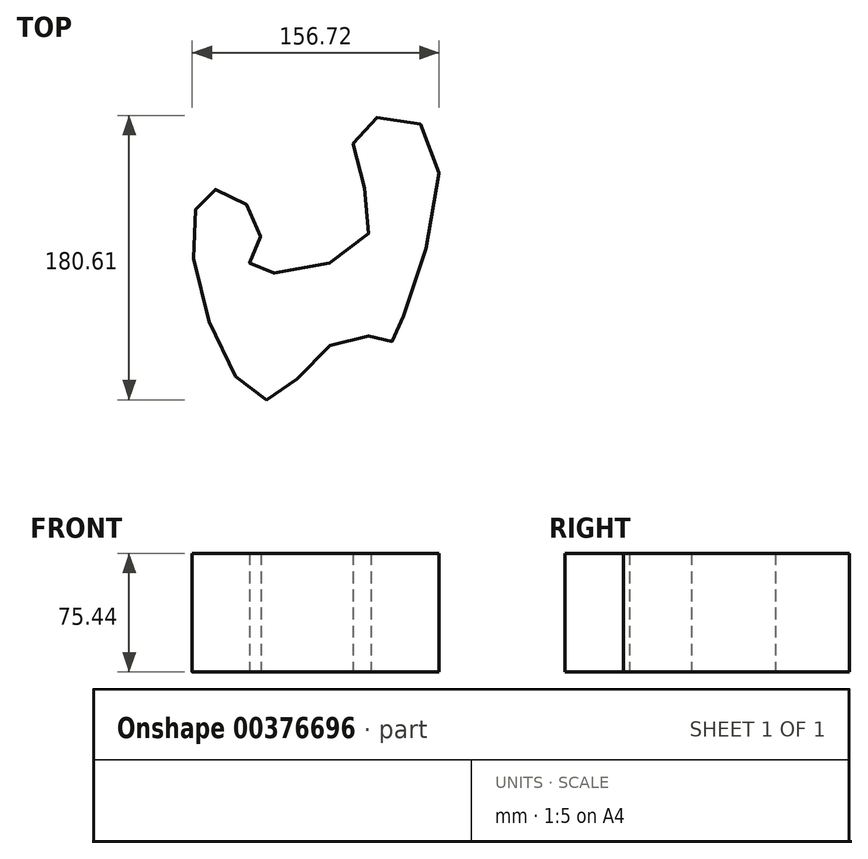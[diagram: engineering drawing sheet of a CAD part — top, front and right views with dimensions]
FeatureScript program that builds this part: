
annotation { "Feature Type Name" : "Feature", "Feature Type Description" : "" }
export const myFeature = defineFeature(function(context is Context, id is Id, definition is map)
    precondition{}
    {
        {
            var Q0;
            Q0=qCreatedBy(makeId("Top.planeOp"),FACE);
            var sketch = newSketch(context, id + "F0", { "sketchPlane" : qUnion([Q0])});
            skFitSpline(sketch, "E0", {"points": [v(-137.83, -57.14) * mm, v(-123.76, -13.3) * mm, v(-95.1, -40.71) * mm, v(-101.2, -63.47) * mm, v(-28.09, -44.15) * mm, v(-34.93, 22.42) * mm, v(13.54, 20.18) * mm, v(-11.02, -109.4) * mm, v(-11.71, -109.8) * mm, v(-44.48, -108.57) * mm, v(-91.93, -146.96) * mm, v(-137.83, -57.14) * mm]});
            skSolve(sketch);
        }
        {
            var Q0;
            Q0=makeQuery(id+"F0.imprint","IMPRINT",FACE,{"disambiguationData":[TD([[makeQuery(id+"F0.imprint","IMPRINT",EDGE,{"derivedFrom":sQuery(id+"F0.wireOp",EDGE,"E0")}),-1.0]])]});
            extrude(context, id + "F1", {"entities" : qUnion([Q0]), "depth" : 75.44 * mm});
        }
    });
